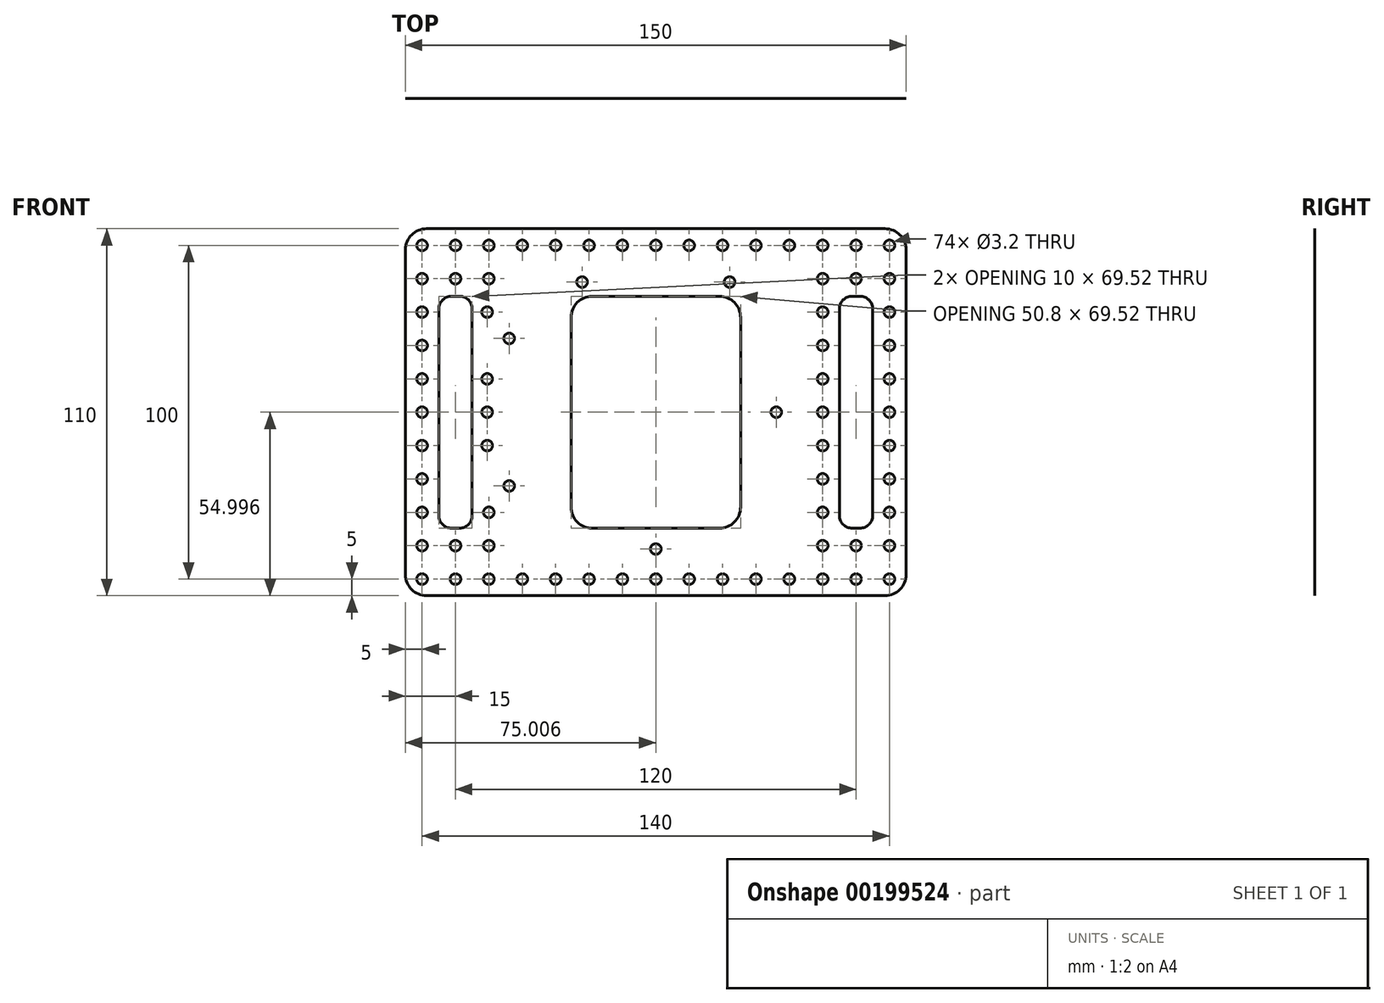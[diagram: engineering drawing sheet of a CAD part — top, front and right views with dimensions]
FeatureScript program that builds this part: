
annotation { "Feature Type Name" : "Feature", "Feature Type Description" : "" }
export const myFeature = defineFeature(function(context is Context, id is Id, definition is map)
    precondition{}
    {
        {
            var Q0;
            Q0=qCreatedBy(makeId("Front.planeOp"),FACE);
            var sketch = newSketch(context, id + "F0", { "sketchPlane" : qUnion([Q0])});
            skLineSegment(sketch, "E0.bottom", {"start": v(6.35, 0) * mm, "end": v(143.65, 0) * mm});
            skLineSegment(sketch, "E0.top", {"start": v(6.35, -110) * mm, "end": v(143.65, -110) * mm});
            skLineSegment(sketch, "E0.left", {"start": v(0, -6.35) * mm, "end": v(0, -103.65) * mm});
            skLineSegment(sketch, "E0.right", {"start": v(150, -6.35) * mm, "end": v(150, -103.65) * mm});
            skLineSegment(sketch, "E1.bottom", {"start": v(13.8, -20.24) * mm, "end": v(16.19, -20.24) * mm});
            skLineSegment(sketch, "E1.top", {"start": v(13.81, -89.76) * mm, "end": v(16.19, -89.76) * mm});
            skLineSegment(sketch, "E1.left", {"start": v(10, -24.05) * mm, "end": v(10, -85.95) * mm});
            skCircle(sketch, "E2", {"center": v(75, -96) * mm, "radius": 1.6 * mm});
            skPoint(sketch, "E2.centerSnap0", {"position": v(75, -110) * mm});
            skCircle(sketch, "E3", {"center": v(52.9, -16) * mm, "radius": 1.6 * mm});
            skCircle(sketch, "E4", {"center": v(97.1, -16) * mm, "radius": 1.6 * mm});
            skLineSegment(sketch, "E5.left", {"start": v(20, -24.05) * mm, "end": v(20, -85.95) * mm});
            skPoint(sketch, "E6.visualSharp", {"position": v(0, 0) * mm});
            skArc(sketch, "E6.filletArc", {"start": v(6.35, 0) * mm, "mid": v(1.86, -1.86) * mm, "end": v(0, -6.35) * mm});
            skPoint(sketch, "E7.visualSharp", {"position": v(0, -110) * mm});
            skArc(sketch, "E7.filletArc", {"start": v(0, -103.65) * mm, "mid": v(1.86, -108.14) * mm, "end": v(6.35, -110) * mm});
            skPoint(sketch, "E8.visualSharp", {"position": v(150, -110) * mm});
            skArc(sketch, "E8.filletArc", {"start": v(143.65, -110) * mm, "mid": v(148.14, -108.14) * mm, "end": v(150, -103.65) * mm});
            skPoint(sketch, "E9.visualSharp", {"position": v(150, 0) * mm});
            skArc(sketch, "E9.filletArc", {"start": v(150, -6.35) * mm, "mid": v(148.14, -1.86) * mm, "end": v(143.65, 0) * mm});
            skLineSegment(sketch, "E10.right", {"start": v(49.6, -26.6) * mm, "end": v(49.6, -83.41) * mm});
            skLineSegment(sketch, "E11.left", {"start": v(100.4, -26.6) * mm, "end": v(100.4, -83.41) * mm});
            skLineSegment(sketch, "E12", {"start": v(55.96, -20.24) * mm, "end": v(94.06, -20.24) * mm});
            skLineSegment(sketch, "E13", {"start": v(55.96, -89.76) * mm, "end": v(94.06, -89.76) * mm});
            skCircle(sketch, "E14", {"center": v(31.08, -32.9) * mm, "radius": 1.6 * mm});
            skCircle(sketch, "E15", {"center": v(111.08, -55) * mm, "radius": 1.6 * mm});
            skCircle(sketch, "E16", {"center": v(31.08, -77.1) * mm, "radius": 1.6 * mm});
            skLineSegment(sketch, "E17.bottom", {"start": v(133.8, -20.24) * mm, "end": v(136.19, -20.24) * mm});
            skLineSegment(sketch, "E17.top", {"start": v(133.8, -89.76) * mm, "end": v(136.19, -89.76) * mm});
            skLineSegment(sketch, "E17.left", {"start": v(130, -24.05) * mm, "end": v(130, -85.95) * mm});
            skLineSegment(sketch, "E17.right", {"start": v(140, -24.05) * mm, "end": v(140, -85.95) * mm});
            skCircle(sketch, "E18", {"center": v(5, -55) * mm, "radius": 1.6 * mm});
            skPoint(sketch, "E18.centerSnap0", {"position": v(0, -55) * mm});
            skCircle(sketch, "E19.0.1.0", {"center": v(5, -45) * mm, "radius": 1.6 * mm});
            skCircle(sketch, "E19.0.2.0", {"center": v(5, -35) * mm, "radius": 1.6 * mm});
            skCircle(sketch, "E19.0.3.0", {"center": v(5, -25) * mm, "radius": 1.6 * mm});
            skCircle(sketch, "E19.0.4.0", {"center": v(5, -15) * mm, "radius": 1.6 * mm});
            skCircle(sketch, "E19.0.5.0", {"center": v(5, -5) * mm, "radius": 1.6 * mm});
            skCircle(sketch, "E20.MirrorC", {"center": v(5, -65) * mm, "radius": 1.6 * mm});
            skCircle(sketch, "E21.MirrorC", {"center": v(5, -75) * mm, "radius": 1.6 * mm});
            skCircle(sketch, "E22.MirrorC", {"center": v(5, -85) * mm, "radius": 1.6 * mm});
            skCircle(sketch, "E23.MirrorC", {"center": v(5, -95) * mm, "radius": 1.6 * mm});
            skCircle(sketch, "E24.MirrorC", {"center": v(5, -105) * mm, "radius": 1.6 * mm});
            skCircle(sketch, "E25.MirrorC", {"center": v(25, -5) * mm, "radius": 1.6 * mm});
            skCircle(sketch, "E26.MirrorC", {"center": v(25, -15) * mm, "radius": 1.6 * mm});
            skCircle(sketch, "E27.MirrorC", {"center": v(24.5, -25) * mm, "radius": 1.6 * mm});
            skCircle(sketch, "E28.MirrorC", {"center": v(25, -85) * mm, "radius": 1.6 * mm});
            skCircle(sketch, "E29.MirrorC", {"center": v(25, -95) * mm, "radius": 1.6 * mm});
            skCircle(sketch, "E30.MirrorC", {"center": v(25, -105) * mm, "radius": 1.6 * mm});
            skCircle(sketch, "E31.MirrorC", {"center": v(125, -5) * mm, "radius": 1.6 * mm});
            skCircle(sketch, "E32.MirrorC", {"center": v(145, -5) * mm, "radius": 1.6 * mm});
            skCircle(sketch, "E33.MirrorC", {"center": v(145, -15) * mm, "radius": 1.6 * mm});
            skCircle(sketch, "E34.MirrorC", {"center": v(125, -15) * mm, "radius": 1.6 * mm});
            skCircle(sketch, "E35", {"center": v(15, -5) * mm, "radius": 1.6 * mm});
            skCircle(sketch, "E36", {"center": v(15, -15) * mm, "radius": 1.6 * mm});
            skCircle(sketch, "E37.MirrorC", {"center": v(15, -95) * mm, "radius": 1.6 * mm});
            skCircle(sketch, "E38.MirrorC", {"center": v(15, -105) * mm, "radius": 1.6 * mm});
            skCircle(sketch, "E39.MirrorC", {"center": v(135, -5) * mm, "radius": 1.6 * mm});
            skCircle(sketch, "E40.MirrorC", {"center": v(135, -15) * mm, "radius": 1.6 * mm});
            skCircle(sketch, "E41.MirrorC", {"center": v(125, -25) * mm, "radius": 1.6 * mm});
            skCircle(sketch, "E42.MirrorC", {"center": v(125, -35) * mm, "radius": 1.6 * mm});
            skCircle(sketch, "E43.MirrorC", {"center": v(125, -45) * mm, "radius": 1.6 * mm});
            skCircle(sketch, "E44.MirrorC", {"center": v(125, -55) * mm, "radius": 1.6 * mm});
            skCircle(sketch, "E45.MirrorC", {"center": v(125, -65) * mm, "radius": 1.6 * mm});
            skCircle(sketch, "E46.MirrorC", {"center": v(125, -75) * mm, "radius": 1.6 * mm});
            skCircle(sketch, "E47.MirrorC", {"center": v(125, -85) * mm, "radius": 1.6 * mm});
            skCircle(sketch, "E48.MirrorC", {"center": v(125, -95) * mm, "radius": 1.6 * mm});
            skCircle(sketch, "E49.MirrorC", {"center": v(125, -105) * mm, "radius": 1.6 * mm});
            skCircle(sketch, "E50.MirrorC", {"center": v(135, -105) * mm, "radius": 1.6 * mm});
            skCircle(sketch, "E51.MirrorC", {"center": v(135, -95) * mm, "radius": 1.6 * mm});
            skCircle(sketch, "E52.MirrorC", {"center": v(145, -95) * mm, "radius": 1.6 * mm});
            skCircle(sketch, "E53.MirrorC", {"center": v(145, -105) * mm, "radius": 1.6 * mm});
            skCircle(sketch, "E54.MirrorC", {"center": v(145, -85) * mm, "radius": 1.6 * mm});
            skCircle(sketch, "E55.MirrorC", {"center": v(145, -75) * mm, "radius": 1.6 * mm});
            skCircle(sketch, "E56.MirrorC", {"center": v(145, -65) * mm, "radius": 1.6 * mm});
            skCircle(sketch, "E57.MirrorC", {"center": v(145, -55) * mm, "radius": 1.6 * mm});
            skCircle(sketch, "E58.MirrorC", {"center": v(145, -45) * mm, "radius": 1.6 * mm});
            skCircle(sketch, "E59.MirrorC", {"center": v(145, -35) * mm, "radius": 1.6 * mm});
            skCircle(sketch, "E60.MirrorC", {"center": v(145, -25) * mm, "radius": 1.6 * mm});
            skCircle(sketch, "E61.1.0.0", {"center": v(35, -105) * mm, "radius": 1.6 * mm});
            skCircle(sketch, "E61.2.0.0", {"center": v(45, -105) * mm, "radius": 1.6 * mm});
            skCircle(sketch, "E61.3.0.0", {"center": v(55, -105) * mm, "radius": 1.6 * mm});
            skCircle(sketch, "E61.4.0.0", {"center": v(65, -105) * mm, "radius": 1.6 * mm});
            skCircle(sketch, "E61.5.0.0", {"center": v(75, -105) * mm, "radius": 1.6 * mm});
            skCircle(sketch, "E61.6.0.0", {"center": v(85, -105) * mm, "radius": 1.6 * mm});
            skCircle(sketch, "E61.7.0.0", {"center": v(95, -105) * mm, "radius": 1.6 * mm});
            skCircle(sketch, "E61.8.0.0", {"center": v(105, -105) * mm, "radius": 1.6 * mm});
            skCircle(sketch, "E61.9.0.0", {"center": v(115, -105) * mm, "radius": 1.6 * mm});
            skLineSegment(sketch, "E61.direction1", {"start": v(25, -105) * mm, "end": v(35, -105) * mm, "construction": true});
            skPoint(sketch, "E62.endSnap0", {"position": v(10, -55) * mm});
            skCircle(sketch, "E63.MirrorC", {"center": v(35, -5) * mm, "radius": 1.6 * mm});
            skCircle(sketch, "E64.MirrorC", {"center": v(45, -5) * mm, "radius": 1.6 * mm});
            skCircle(sketch, "E65.MirrorC", {"center": v(55, -5) * mm, "radius": 1.6 * mm});
            skCircle(sketch, "E66.MirrorC", {"center": v(65, -5) * mm, "radius": 1.6 * mm});
            skCircle(sketch, "E67.MirrorC", {"center": v(75, -5) * mm, "radius": 1.6 * mm});
            skCircle(sketch, "E68.MirrorC", {"center": v(85, -5) * mm, "radius": 1.6 * mm});
            skCircle(sketch, "E69.MirrorC", {"center": v(95, -5) * mm, "radius": 1.6 * mm});
            skCircle(sketch, "E70.MirrorC", {"center": v(105, -5) * mm, "radius": 1.6 * mm});
            skCircle(sketch, "E71.MirrorC", {"center": v(115, -5) * mm, "radius": 1.6 * mm});
            skPoint(sketch, "E72.visualSharp", {"position": v(49.6, -20.24) * mm});
            skArc(sketch, "E72.filletArc", {"start": v(55.96, -20.24) * mm, "mid": v(51.47, -22.1) * mm, "end": v(49.6, -26.6) * mm});
            skPoint(sketch, "E73.visualSharp", {"position": v(100.4, -89.76) * mm});
            skArc(sketch, "E73.filletArc", {"start": v(94.06, -89.76) * mm, "mid": v(98.55, -87.9) * mm, "end": v(100.4, -83.41) * mm});
            skPoint(sketch, "E74.visualSharp", {"position": v(49.6, -89.76) * mm});
            skArc(sketch, "E74.filletArc", {"start": v(49.6, -83.41) * mm, "mid": v(51.47, -87.9) * mm, "end": v(55.96, -89.76) * mm});
            skPoint(sketch, "E75.visualSharp", {"position": v(100.4, -20.24) * mm});
            skArc(sketch, "E75.filletArc", {"start": v(100.4, -26.6) * mm, "mid": v(98.55, -22.1) * mm, "end": v(94.06, -20.24) * mm});
            skPoint(sketch, "E76.visualSharp", {"position": v(10, -20.24) * mm});
            skArc(sketch, "E76.filletArc", {"start": v(13.8, -20.24) * mm, "mid": v(11.12, -21.36) * mm, "end": v(10, -24.05) * mm});
            skPoint(sketch, "E77.visualSharp", {"position": v(20, -20.24) * mm});
            skArc(sketch, "E77.filletArc", {"start": v(20, -24.05) * mm, "mid": v(18.88, -21.36) * mm, "end": v(16.19, -20.24) * mm});
            skPoint(sketch, "E78.visualSharp", {"position": v(10, -89.76) * mm});
            skArc(sketch, "E78.filletArc", {"start": v(10, -85.95) * mm, "mid": v(11.12, -88.65) * mm, "end": v(13.81, -89.76) * mm});
            skPoint(sketch, "E79.visualSharp", {"position": v(20, -89.76) * mm});
            skArc(sketch, "E79.filletArc", {"start": v(16.19, -89.76) * mm, "mid": v(18.88, -88.65) * mm, "end": v(20, -85.95) * mm});
            skPoint(sketch, "E80.visualSharp", {"position": v(130, -89.76) * mm});
            skArc(sketch, "E80.filletArc", {"start": v(130, -85.95) * mm, "mid": v(131.12, -88.65) * mm, "end": v(133.8, -89.76) * mm});
            skPoint(sketch, "E81.visualSharp", {"position": v(140, -89.76) * mm});
            skArc(sketch, "E81.filletArc", {"start": v(136.19, -89.76) * mm, "mid": v(138.88, -88.65) * mm, "end": v(140, -85.95) * mm});
            skPoint(sketch, "E82.visualSharp", {"position": v(140, -20.24) * mm});
            skArc(sketch, "E82.filletArc", {"start": v(140, -24.05) * mm, "mid": v(138.88, -21.36) * mm, "end": v(136.19, -20.24) * mm});
            skPoint(sketch, "E83.visualSharp", {"position": v(130, -20.24) * mm});
            skArc(sketch, "E83.filletArc", {"start": v(133.8, -20.24) * mm, "mid": v(131.12, -21.36) * mm, "end": v(130, -24.05) * mm});
            skCircle(sketch, "E84.0.2.0", {"center": v(24.5, -45) * mm, "radius": 1.6 * mm});
            skCircle(sketch, "E84.0.3.0", {"center": v(24.5, -55) * mm, "radius": 1.6 * mm});
            skCircle(sketch, "E84.0.4.0", {"center": v(24.5, -65) * mm, "radius": 1.6 * mm});
            skLineSegment(sketch, "E84.direction1", {"start": v(24.5, -25) * mm, "end": v(50.4, -25) * mm, "construction": true});
            skLineSegment(sketch, "E84.direction2", {"start": v(24.5, -25) * mm, "end": v(24.5, -35) * mm, "construction": true});
            skSolve(sketch);
        }
        {
            var Q0;
            Q0=makeQuery(id+"F0.imprint","IMPRINT",FACE,{"disambiguationData":[TD([[makeQuery(id+"F0.imprint","IMPRINT",EDGE,{"derivedFrom":sQuery(id+"F0.wireOp",EDGE,"E0.bottom")}),-1.0]])]});
            extrude(context, id + "F1", {"entities" : qUnion([Q0]), "depth" : 1 / 203.2 * mm});
        }
    });
